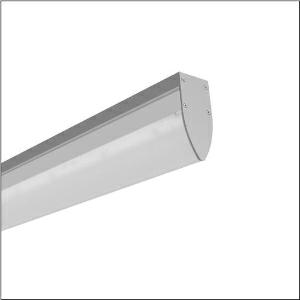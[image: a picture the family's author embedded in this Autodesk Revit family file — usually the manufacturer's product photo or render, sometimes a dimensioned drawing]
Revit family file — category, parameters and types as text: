
# Revit family: mira_r__21_td_51fr527g434a_c56a
name_source: partatom
category: Lighting Fixtures
units: mm (PartAtom-declared; Revit-internal decimal feet)

## family parameters
Cut with Voids When Loaded = No
Host = Face
Light Source = No
Part Type = Normal
Room Calculation Point = No
Round Connector Dimension = Use Diameter
Shared = No

## types (1)
- Mira® 21 TD (1 x LED, 3020 lm, 20 W, 4000K)
    Apparent Load = 20 VA
    CIE Flux Codes = 40 68 87 81 100
    Color Rendering = 80
    Color Temperature = 4000K
    Default Elevation = 1800 mm
    Description = Mira® 21 TD, clean room luminaire, primary light control with reflector, primary optical cover: cover, of PMMA, frosted, light emission: direct distribution, primary light characteristic: symmetric, installation type: surface-mounted, LED, rated luminous flux: 3.020lm, luminous efficacy: 151lm/W, light colour: 840, colour temperature: 4000K, control gear: ECG, with terminal, 3-pole, max. 2.5mm², mains connection: 230V, AC, 50/60Hz, rated input power: 20W, luminaire housing, of sheet steel, coated, pure white (RAL 9010), length: 900mm, width: 55mm, height: 120mm, protection rating (complete): IP43, insulation class (complete): insulation class I (protective earthing), certification: CE, UKCA, permissible operating ambient temperature: -5..+40°C, standard: EN 50419, packaging unit: 1 piece
    Height = 0 mm  [stored 0 ft]
    Lamp = 1 x LED
    Lamp Light Flux = 3020 lm
    Lamp Power = 20 W
    Lamp count = 1
    Length = 900 mm
    Luminous efficacy = 151 lm/W
    Manufacturer = Siteco
    ModVariant = No
    Model = 51FR527G434A
    Mounting Place = Ceiling
    Mounting Type = Recessed
    Number of Poles = 1
    OnlyDefault = Yes
    Power Factor = 1
    Product Name = Mira® 21 TD
    Product group = clean room luminaire
    ProductGroupID = 402
    Protection Class = Protection class I
    Protection Degree = IP 43
    RLX_Detail_Level = 1
    RLX_Emergency_Light_Flux = 0 lm
    RLX_Emergency_Type = 0
    RLX_Emergency_Type_DB = No
    RlxData = <blob elided: 25097 chars, md5=50a709e0>
    Socket = socket
    Standby Power = 0 W
    System Light Flux = 3020 lm
    System Power = 20 W
    Type Comments = Product without accessories
    Type Image = l_1007115.jpg
    URL = http://relux.com
    VarID = ---
    Voltage = 0 V
    Weight = 0.00 kg
    Width = 55 mm

note: [stored X ft] marks values corroborated as IEEE doubles in the binary element streams (Revit-internal decimal feet)

## geometry (parser evidence)
native form markers: Blend x4, Sweep x11
no freeform markers — native parametric forms only
